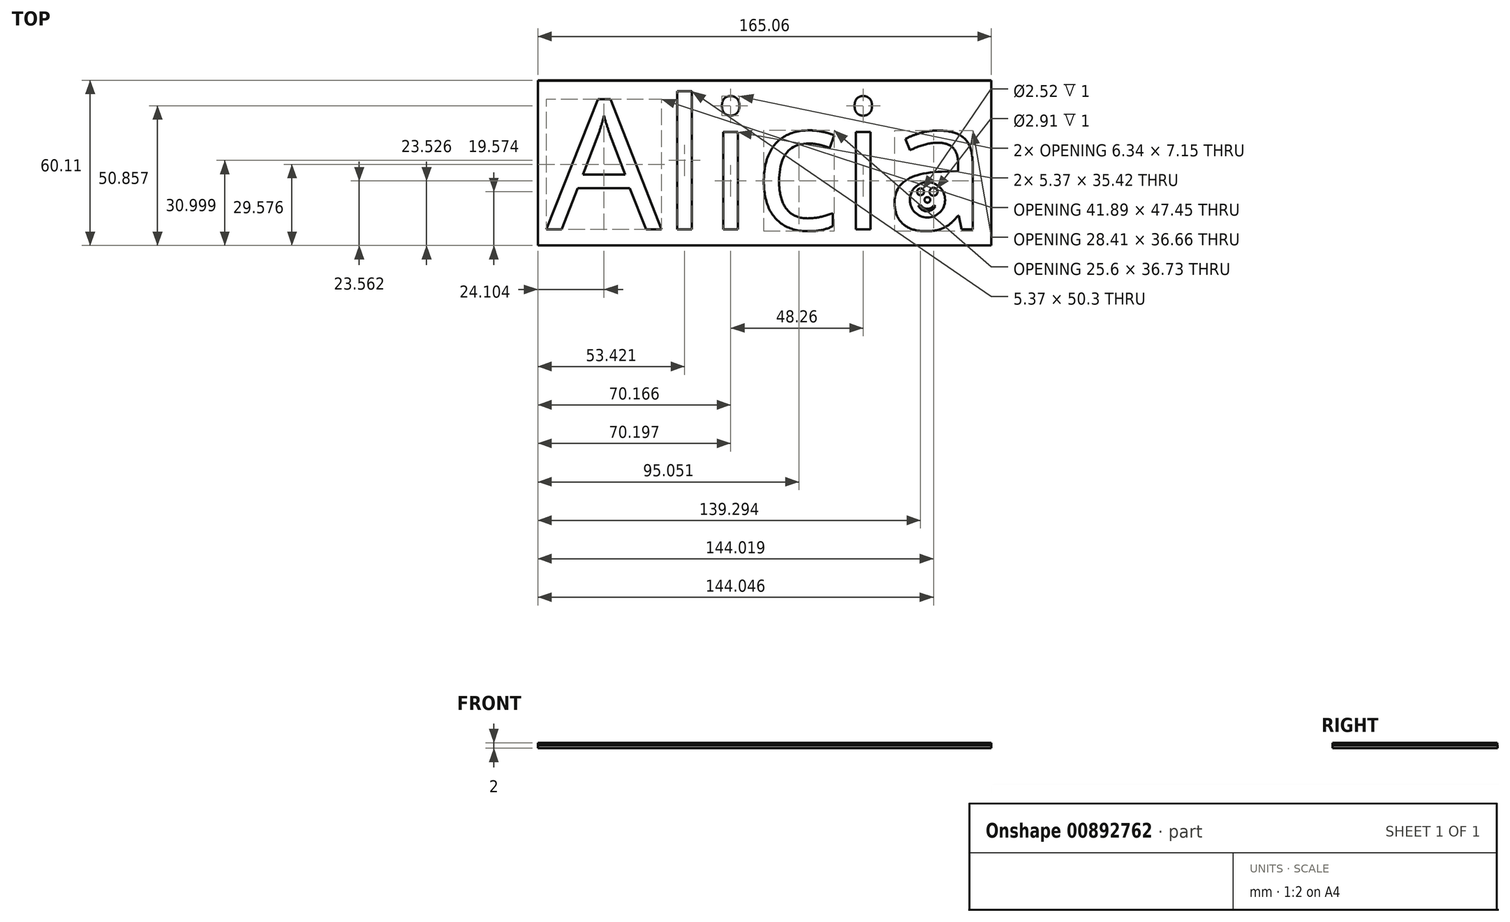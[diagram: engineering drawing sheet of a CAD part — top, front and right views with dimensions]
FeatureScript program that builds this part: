
annotation { "Feature Type Name" : "Feature", "Feature Type Description" : "" }
export const myFeature = defineFeature(function(context is Context, id is Id, definition is map)
    precondition{}
    {
        {
            var Q0;
            Q0=qCreatedBy(makeId("Top.planeOp"),FACE);
            var sketch = newSketch(context, id + "F0", { "sketchPlane" : qUnion([Q0])});
            skLineSegment(sketch, "E0.bottom", {"start": v(-83.15, 28.7) * mm, "end": v(81.85, 28.7) * mm});
            skLineSegment(sketch, "E0.top", {"start": v(-83.15, -31.3) * mm, "end": v(81.85, -31.3) * mm});
            skLineSegment(sketch, "E0.left", {"start": v(-83.15, 28.7) * mm, "end": v(-83.15, -31.3) * mm});
            skLineSegment(sketch, "E0.right", {"start": v(81.85, 28.7) * mm, "end": v(81.85, -31.3) * mm});
            skText(sketch, "E1", { "text": "Alicia", "fontName": "OpenSans-Regular.ttf"});
            const initialGuessF0  = {"E1": [-0.07999, -0.02546, 1, 0, 0.04766]};
            skSetInitialGuess(sketch, initialGuessF0);
            skSolve(sketch);
        }
        {
            var Q0;
            Q0 = qSketchRegion(id + "F0", true);
            var Q1;
            Q1=makeQuery(id+"F0.imprint","IMPRINT",FACE,{"disambiguationData":[TD([[makeQuery(id+"F0.imprint","IMPRINT",EDGE,{"derivedFrom":sQuery(id+"F0.wireOp",EDGE,"E1.sketch_text.stroke-8")}),1.0]])]});
            extrude(context, id + "F1", {"entities" : qUnion([Q0, Q1]), "depth" : 1 * mm, "offsetDistance" : 25.4 * mm});
        }
        {
            var Q0;
            Q0=qCreatedBy(makeId("Top.planeOp"),FACE);
            var sketch = newSketch(context, id + "F2", { "sketchPlane" : qUnion([Q0])});
            skLineSegment(sketch, "E2.bottom", {"start": v(-83.07, -31.26) * mm, "end": v(81.91, -31.26) * mm});
            skLineSegment(sketch, "E2.top", {"start": v(-83.07, 28.8) * mm, "end": v(81.91, 28.8) * mm});
            skLineSegment(sketch, "E2.left", {"start": v(-83.07, -31.26) * mm, "end": v(-83.07, 28.8) * mm});
            skLineSegment(sketch, "E2.right", {"start": v(81.91, -31.26) * mm, "end": v(81.91, 28.8) * mm});
            skSolve(sketch);
        }
        {
            var Q0;
            Q0 = qSketchRegion(id + "F2", true);
            extrude(context, id + "F3", {"entities" : qUnion([Q0]), "oppositeDirection" : true, "depth" : 1 * mm, "offsetDistance" : 25.4 * mm});
        }
        {
            var Q0;
            Q0=qCreatedBy(makeId("Top.planeOp"),FACE);
            var sketch = newSketch(context, id + "F4", { "sketchPlane" : qUnion([Q0])});
            skCircle(sketch, "E3", {"center": v(58.65, -14.69) * mm, "radius": 6.4 * mm});
            skCircle(sketch, "E4", {"center": v(56.14, -11.74) * mm, "radius": 1.26 * mm});
            skCircle(sketch, "E5", {"center": v(60.87, -11.74) * mm, "radius": 1.45 * mm});
            skArc(sketch, "E6", {"start": v(56.14, -16.46) * mm, "mid": v(58.54, -17.95) * mm, "end": v(61.02, -16.61) * mm});
            skLineSegment(sketch, "E7", {"start": v(61.02, -16.61) * mm, "end": v(61.56, -17) * mm});
            skLineSegment(sketch, "E8", {"start": v(56.14, -16.46) * mm, "end": v(55.4, -16.8) * mm});
            skArc(sketch, "E9", {"start": v(55.4, -16.8) * mm, "mid": v(58.42, -18.85) * mm, "end": v(61.56, -17) * mm});
            skCircle(sketch, "E10", {"center": v(58.65, -14.69) * mm, "radius": 1.02 * mm});
            skSolve(sketch);
        }
        {
            var Q0;
            Q0=makeQuery(id+"F4.imprint","IMPRINT",FACE,{"disambiguationData":[TD([[makeQuery(id+"F4.imprint","IMPRINT",EDGE,{"derivedFrom":sQuery(id+"F4.wireOp",EDGE,"E3")}),1.0]])]});
            extrude(context, id + "F5", {"entities" : qUnion([Q0]), "operationType" : NewBodyOperationType.ADD, "depth" : 1 * mm, "offsetDistance" : 25.4 * mm});
        }
    });
